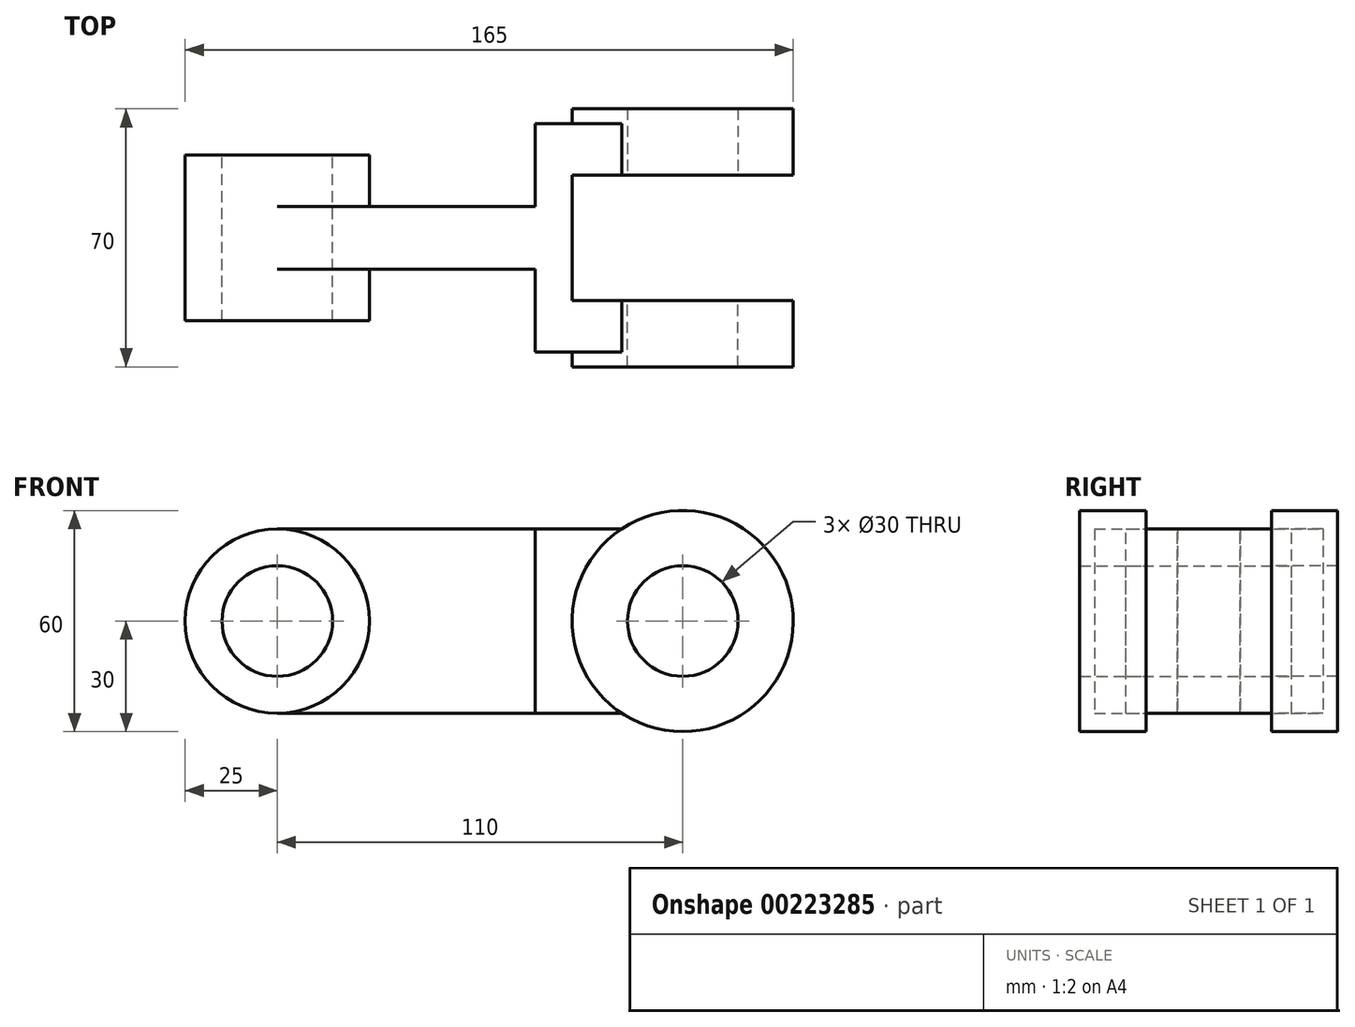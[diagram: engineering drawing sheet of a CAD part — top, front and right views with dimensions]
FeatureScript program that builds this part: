
annotation { "Feature Type Name" : "Feature", "Feature Type Description" : "" }
export const myFeature = defineFeature(function(context is Context, id is Id, definition is map)
    precondition{}
    {
        {
            var Q0;
            Q0=qCreatedBy(makeId("Front.planeOp"),FACE);
            var sketch = newSketch(context, id + "F0", { "sketchPlane" : qUnion([Q0])});
            skCircle(sketch, "E0", {"center": v(0, 0) * mm, "radius": 25 * mm});
            skCircle(sketch, "E1", {"center": v(0, 0) * mm, "radius": 15 * mm});
            skLineSegment(sketch, "E2.bottom", {"start": v(0, 25) * mm, "end": v(70, 25) * mm});
            skLineSegment(sketch, "E2.top", {"start": v(0, -25) * mm, "end": v(70, -25) * mm});
            skLineSegment(sketch, "E2.left", {"start": v(0, 25) * mm, "end": v(0, -25) * mm});
            skLineSegment(sketch, "E2.right", {"start": v(70, 25) * mm, "end": v(70, -25) * mm});
            skLineSegment(sketch, "E3", {"start": v(70, 25) * mm, "end": v(80, 25) * mm});
            skLineSegment(sketch, "E4", {"start": v(80, 25) * mm, "end": v(80, -25) * mm});
            skLineSegment(sketch, "E5", {"start": v(80, -25) * mm, "end": v(70, -25) * mm});
            skSolve(sketch);
        }
        {
            var Q0;
            {var subQ0=sQuery(id+"F0.wireOp",EDGE,"E2.left");var subQ4=sQuery(id+"F0.wireOp",EDGE,"E1");var subQ5=makeQuery(id+"F0.imprint","INTERSECT",VERTEX,{"disambiguationData":[OD(0.0)],"derivedFrom":[subQ4,subQ0]});Q0=makeQuery(id+"F0.imprint","IMPRINT",FACE,{"disambiguationData":[TD([[makeQuery(id+"F0.imprint","IMPRINT",EDGE,{"disambiguationData":[TD([[subQ5,-1.0]])],"derivedFrom":subQ4}),-1.0]])]});}
            var Q1;
            {var subQ0=sQuery(id+"F0.wireOp",EDGE,"E2.left");var subQ4=sQuery(id+"F0.wireOp",EDGE,"E1");var subQ5=makeQuery(id+"F0.imprint","INTERSECT",VERTEX,{"disambiguationData":[OD(0.0)],"derivedFrom":[subQ4,subQ0]});Q1=makeQuery(id+"F0.imprint","IMPRINT",FACE,{"disambiguationData":[TD([[makeQuery(id+"F0.imprint","IMPRINT",EDGE,{"disambiguationData":[TD([[subQ5,1.0]])],"derivedFrom":subQ4}),-1.0]])]});}
            extrude(context, id + "F1", {"entities" : qUnion([Q0, Q1]), "endBound" : BoundingType.SYMMETRIC, "depth" : 45 * mm});
        }
        {
            var Q0;
            {var subQ1=sQuery(id+"F0.wireOp",EDGE,"E2.bottom");Q0=makeQuery(id+"F0.imprint","IMPRINT",FACE,{"disambiguationData":[TD([[makeQuery(id+"F0.imprint","IMPRINT",EDGE,{"derivedFrom":subQ1}),-1.0]])]});}
            extrude(context, id + "F2", {"entities" : qUnion([Q0]), "operationType" : NewBodyOperationType.ADD, "endBound" : BoundingType.SYMMETRIC, "depth" : 17 * mm});
        }
        {
            var Q0;
            Q0=makeQuery(id+"F0.imprint","IMPRINT",FACE,{"disambiguationData":[TD([[makeQuery(id+"F0.imprint","IMPRINT",EDGE,{"derivedFrom":sQuery(id+"F0.wireOp",EDGE,"E2.right")}),1.0]])]});
            extrude(context, id + "F3", {"entities" : qUnion([Q0]), "operationType" : NewBodyOperationType.ADD, "endBound" : BoundingType.SYMMETRIC, "depth" : 34 * mm});
        }
        {
            var Q0;
            Q0=makeQuery(id+"F3.opExtrude","CAP_FACE",FACE,{"disambiguationData":[OSD([sQuery(id+"F0.wireOp",EDGE,"E2.right"),sQuery(id+"F0.wireOp",EDGE,"E3"),sQuery(id+"F0.wireOp",EDGE,"E4"),sQuery(id+"F0.wireOp",EDGE,"E5")])],"isStart":false});
            cPlane(context, id + "F4", {"entities" : qUnion([Q0]), "cplaneType" : CPlaneType.OFFSET, "offset" : 0 * mm, "width" : 150 * mm, "height" : 150 * mm});
        }
        {
            var Q0;
            Q0=qCreatedBy(id+"F4.planeOp",FACE);
            var sketch = newSketch(context, id + "F5", { "sketchPlane" : qUnion([Q0])});
            skLineSegment(sketch, "E6.0", {"start": v(70, 25) * mm, "end": v(70, -25) * mm});
            skLineSegment(sketch, "E7", {"start": v(70, 25) * mm, "end": v(110, 25) * mm});
            skLineSegment(sketch, "E8", {"start": v(110, 25) * mm, "end": v(110, -25) * mm});
            skLineSegment(sketch, "E9", {"start": v(110, -25) * mm, "end": v(70, -25) * mm});
            skCircle(sketch, "E10", {"center": v(110, 0) * mm, "radius": 30 * mm});
            skCircle(sketch, "E11", {"center": v(110, 0) * mm, "radius": 15 * mm});
            skSolve(sketch);
        }
        {
            var Q0;
            {var subQ0=sQuery(id+"F5.wireOp",EDGE,"E6.0");Q0=makeQuery(id+"F5.imprint","IMPRINT",FACE,{"disambiguationData":[TD([[makeQuery(id+"F5.imprint","IMPRINT",EDGE,{"derivedFrom":subQ0}),1.0]])]});}
            extrude(context, id + "F6", {"entities" : qUnion([Q0]), "operationType" : NewBodyOperationType.ADD, "depth" : 14 * mm});
        }
        {
            var Q0;
            {var subQ1=sQuery(id+"F5.wireOp",EDGE,"E8");var subQ6=sQuery(id+"F5.wireOp",EDGE,"E7");var subQ9=makeQuery(id+"F5.imprint","INTERSECT",VERTEX,{"derivedFrom":[subQ6,subQ1]});Q0=makeQuery(id+"F5.imprint","IMPRINT",FACE,{"disambiguationData":[TD([[makeQuery(id+"F5.imprint","IMPRINT",EDGE,{"disambiguationData":[TD([[subQ9,1.0]])],"derivedFrom":subQ6}),-1.0]])]});}
            var Q1;
            {var subQ1=sQuery(id+"F5.wireOp",EDGE,"E8");var subQ5=sQuery(id+"F5.wireOp",EDGE,"E7");var subQ6=makeQuery(id+"F5.imprint","INTERSECT",VERTEX,{"derivedFrom":[subQ5,subQ1]});Q1=makeQuery(id+"F5.imprint","IMPRINT",FACE,{"disambiguationData":[TD([[makeQuery(id+"F5.imprint","IMPRINT",EDGE,{"disambiguationData":[TD([[subQ6,1.0]])],"derivedFrom":subQ5}),1.0]])]});}
            extrude(context, id + "F7", {"entities" : qUnion([Q0, Q1]), "operationType" : NewBodyOperationType.ADD, "depth" : 18 * mm});
        }
        {
            var Q0;
            Q0=makeQuery(id+"F1.opExtrude","SWEPT_BODY",BODY,{"disambiguationData":[OSD([sQuery(id+"F0.wireOp",EDGE,"E0"),sQuery(id+"F0.wireOp",EDGE,"E1")])]});
            var Q1;
            Q1=qCreatedBy(makeId("Front.planeOp"),FACE);
            mirror(context, id + "F8", {"operationType" : NewBodyOperationType.ADD, "entities" : qUnion([Q0]), "mirrorPlane" : qUnion([Q1])});
        }
    });
